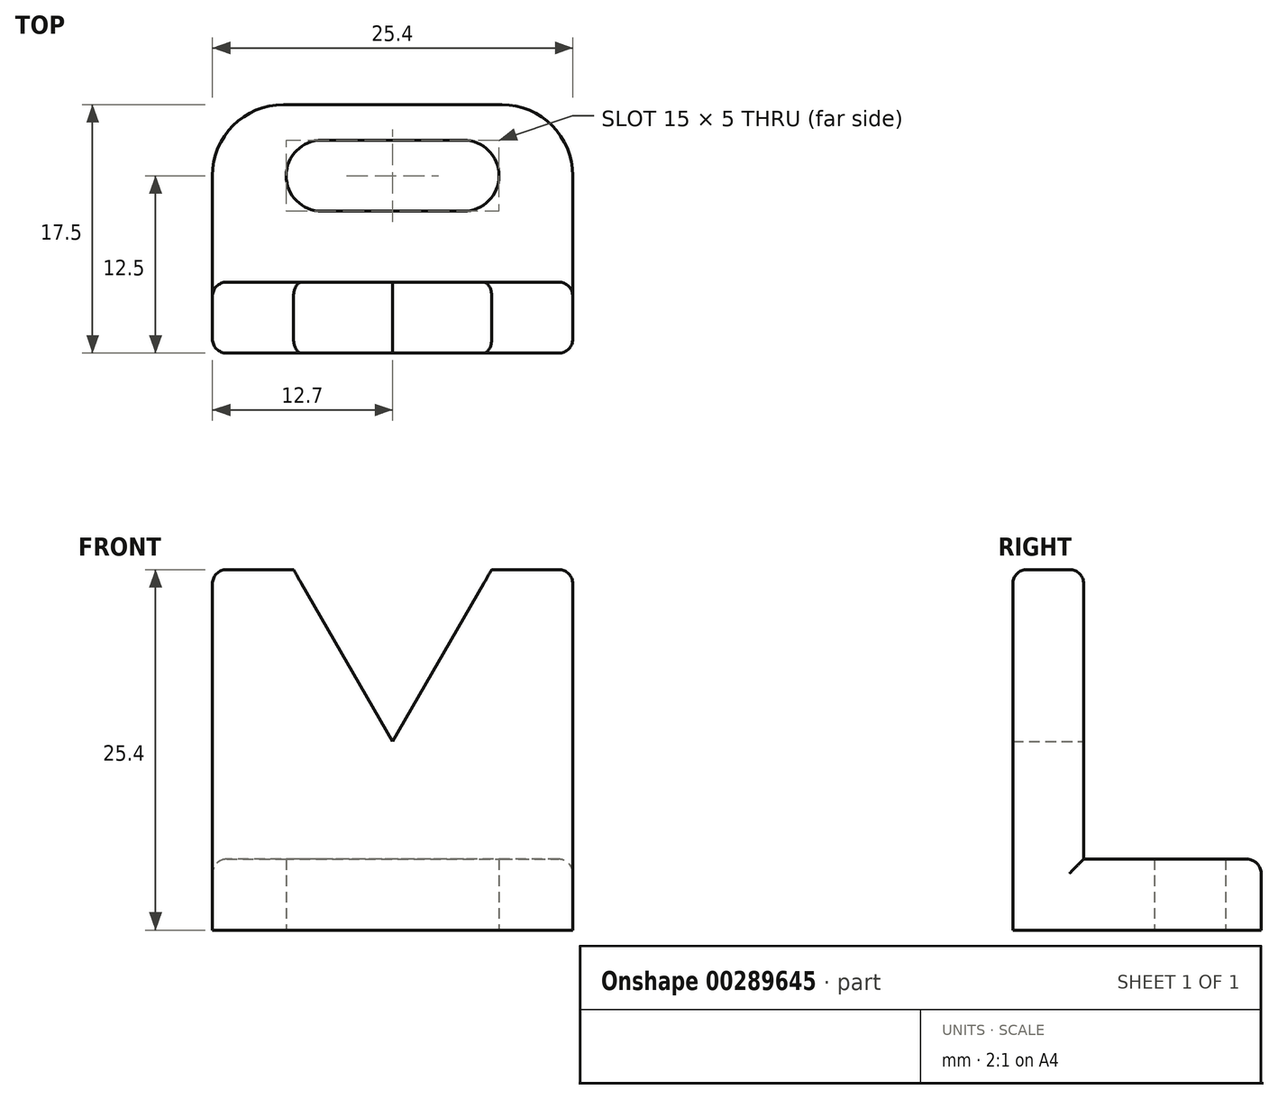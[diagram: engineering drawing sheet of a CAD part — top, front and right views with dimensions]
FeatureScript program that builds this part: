
annotation { "Feature Type Name" : "Feature", "Feature Type Description" : "" }
export const myFeature = defineFeature(function(context is Context, id is Id, definition is map)
    precondition{}
    {
        {
            var Q0;
            Q0=qCreatedBy(makeId("Front.planeOp"),FACE);
            var sketch = newSketch(context, id + "F0", { "sketchPlane" : qUnion([Q0])});
            skLineSegment(sketch, "E0", {"start": v(-12.7, -1.9) * mm, "end": v(-6.98, -1.9) * mm});
            skLineSegment(sketch, "E1", {"start": v(-6.98, -1.9) * mm, "end": v(0, -14) * mm});
            skLineSegment(sketch, "E2", {"start": v(0, -14) * mm, "end": v(6.99, -1.9) * mm});
            skLineSegment(sketch, "E3", {"start": v(6.99, -1.9) * mm, "end": v(12.7, -1.9) * mm});
            skLineSegment(sketch, "E4", {"start": v(12.7, -1.9) * mm, "end": v(12.7, -27.3) * mm});
            skLineSegment(sketch, "E5", {"start": v(12.7, -27.3) * mm, "end": v(-12.7, -27.3) * mm});
            skLineSegment(sketch, "E6", {"start": v(-12.7, -27.3) * mm, "end": v(-12.7, -1.9) * mm});
            skSolve(sketch);
        }
        {
            var Q0;
            Q0=makeQuery(id+"F0.imprint","IMPRINT",FACE,{"disambiguationData":[TD([[makeQuery(id+"F0.imprint","IMPRINT",EDGE,{"derivedFrom":sQuery(id+"F0.wireOp",EDGE,"E0")}),-1.0]])]});
            extrude(context, id + "F1", {"entities" : qUnion([Q0]), "endBound" : BoundingType.SYMMETRIC, "depth" : 5 * mm});
        }
        {
            var Q0;
            Q0=makeQuery(id+"F1.opExtrude","SWEPT_FACE",FACE,{"disambiguationData":[OSD([sQuery(id+"F0.wireOp",EDGE,"E5")])]});
            var sketch = newSketch(context, id + "F2", { "sketchPlane" : qUnion([Q0])});
            skLineSegment(sketch, "E7.MirrorCS", {"start": v(-7.7, -15) * mm, "end": v(7.7, -15) * mm});
            skLineSegment(sketch, "E8.MirrorCS", {"start": v(12.7, -10) * mm, "end": v(12.7, -2.5) * mm});
            skArc(sketch, "E9.MirrorCS", {"start": v(5, -7.5) * mm, "mid": v(7.5, -10) * mm, "end": v(5, -12.5) * mm});
            skLineSegment(sketch, "E10.MirrorCS", {"start": v(-19.05, -10) * mm, "end": v(19.05, -10) * mm, "construction": true});
            skLineSegment(sketch, "E11.MirrorCS", {"start": v(5, -12.5) * mm, "end": v(-5, -12.5) * mm});
            skLineSegment(sketch, "E12.MirrorCS", {"start": v(-5, -7.5) * mm, "end": v(5, -7.5) * mm});
            skArc(sketch, "E13.MirrorCS", {"start": v(-5, -12.5) * mm, "mid": v(-7.5, -10) * mm, "end": v(-5, -7.5) * mm});
            skLineSegment(sketch, "E14.MirrorCS", {"start": v(-12.7, -2.5) * mm, "end": v(-12.7, -10) * mm});
            skPoint(sketch, "E15.visualSharp", {"position": v(-12.7, -15) * mm});
            skArc(sketch, "E15.filletArc", {"start": v(-12.7, -10) * mm, "mid": v(-11.24, -13.54) * mm, "end": v(-7.7, -15) * mm});
            skPoint(sketch, "E16.visualSharp", {"position": v(12.7, -15) * mm});
            skArc(sketch, "E16.filletArc", {"start": v(7.7, -15) * mm, "mid": v(11.24, -13.54) * mm, "end": v(12.7, -10) * mm});
            skSolve(sketch);
        }
        {
            var Q0;
            Q0=makeQuery(id+"F2.imprint","IMPRINT",FACE,{"disambiguationData":[TD([[makeQuery(id+"F2.imprint","IMPRINT",EDGE,{"derivedFrom":sQuery(id+"F2.wireOp",EDGE,"TJxBvZ7U-UePG-uweu-HfqG-7UZ9U8kYDkAn")}),-1.0]])]});
            var Q1;
            Q1=makeQuery(id+"F2.imprint","IMPRINT",FACE,{"disambiguationData":[TD([[makeQuery(id+"F2.imprint","IMPRINT",EDGE,{"derivedFrom":sQuery(id+"F2.wireOp",EDGE,"E7.MirrorCS")}),1.0]])]});
            extrude(context, id + "F3", {"entities" : qUnion([Q0, Q1]), "operationType" : NewBodyOperationType.ADD, "oppositeDirection" : true, "depth" : 5 * mm});
        }
        {
            var Q0;
            Q0=makeQuery(id+"F1.opExtrude","CAP_EDGE",EDGE,{"disambiguationData":[OSD([sQuery(id+"F0.wireOp",EDGE,"E6")])],"isStart":false});
            var Q1;
            Q1=makeQuery(id+"F1.opExtrude","CAP_EDGE",EDGE,{"disambiguationData":[OSD([sQuery(id+"F0.wireOp",EDGE,"E0")])],"isStart":false});
            var Q2;
            Q2=makeQuery(id+"F1.opExtrude","SWEPT_EDGE",EDGE,{"disambiguationData":[OSD([sQuery(id+"F0.wireOp",EDGE,"E0"),sQuery(id+"F0.wireOp",EDGE,"E6")])]});
            var Q3;
            Q3=makeQuery(id+"F1.opExtrude","CAP_EDGE",EDGE,{"disambiguationData":[OSD([sQuery(id+"F0.wireOp",EDGE,"E0")])],"isStart":true});
            var Q4;
            Q4=makeQuery(id+"F1.opExtrude","CAP_EDGE",EDGE,{"disambiguationData":[OSD([sQuery(id+"F0.wireOp",EDGE,"E6")])],"isStart":true});
            var Q5;
            Q5=makeQuery(id+"F3.opExtrude","CAP_EDGE",EDGE,{"disambiguationData":[OSD([sQuery(id+"F2.wireOp",EDGE,"E14.MirrorCS")])],"isStart":false});
            var Q6;
            Q6=makeQuery(id+"F1.opExtrude","CAP_EDGE",EDGE,{"disambiguationData":[OSD([sQuery(id+"F0.wireOp",EDGE,"E4")])],"isStart":true});
            var Q7;
            Q7=makeQuery(id+"F1.opExtrude","CAP_EDGE",EDGE,{"disambiguationData":[OSD([sQuery(id+"F0.wireOp",EDGE,"E4")])],"isStart":false});
            var Q8;
            Q8=makeQuery(id+"F1.opExtrude","SWEPT_EDGE",EDGE,{"disambiguationData":[OSD([sQuery(id+"F0.wireOp",EDGE,"E3"),sQuery(id+"F0.wireOp",EDGE,"E4")])]});
            var Q9;
            Q9=makeQuery(id+"F1.opExtrude","CAP_EDGE",EDGE,{"disambiguationData":[OSD([sQuery(id+"F0.wireOp",EDGE,"E3")])],"isStart":true});
            var Q10;
            Q10=makeQuery(id+"F1.opExtrude","CAP_EDGE",EDGE,{"disambiguationData":[OSD([sQuery(id+"F0.wireOp",EDGE,"E3")])],"isStart":false});
            fillet(context, id + "F4", {"entities" : qUnion([Q0, Q1, Q2, Q3, Q4, Q5, Q6, Q7, Q8, Q9, Q10]), "radius" : 1 * mm, "tangentPropagation" : true, "allowEdgeOverflow" : false});
        }
    });
